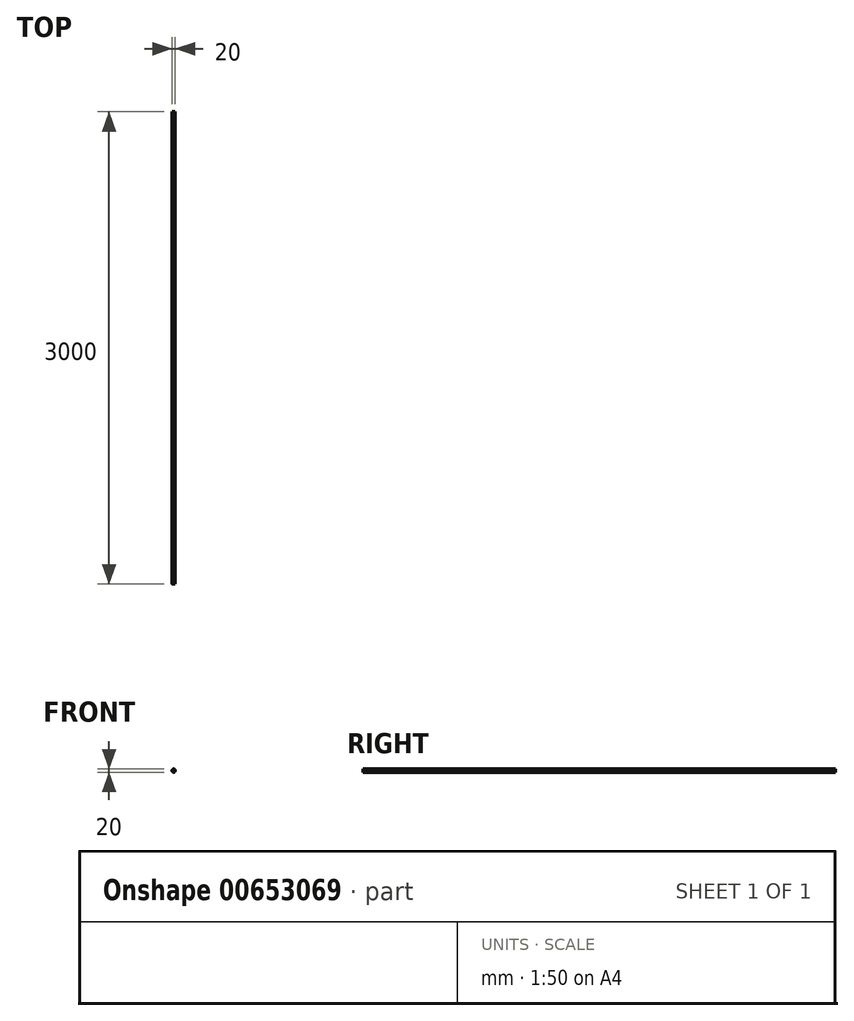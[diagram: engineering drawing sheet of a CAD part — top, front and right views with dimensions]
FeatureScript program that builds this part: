
annotation { "Feature Type Name" : "Feature", "Feature Type Description" : "" }
export const myFeature = defineFeature(function(context is Context, id is Id, definition is map)
    precondition{}
    {
        {
            var Q0;
            Q0=qCreatedBy(makeId("Front.planeOp"),FACE);
            var sketch = newSketch(context, id + "F0", { "sketchPlane" : qUnion([Q0])});
            skCircle(sketch, "E0", {"center": v(0, 0) * mm, "radius": 10 * mm});
            skSolve(sketch);
        }
        {
            var Q0;
            Q0 = qSketchRegion(id + "F0", true);
            extrude(context, id + "F1", {"entities" : qUnion([Q0]), "depth" : 3000 * mm, "offsetDistance" : 25 * mm});
        }
    });
